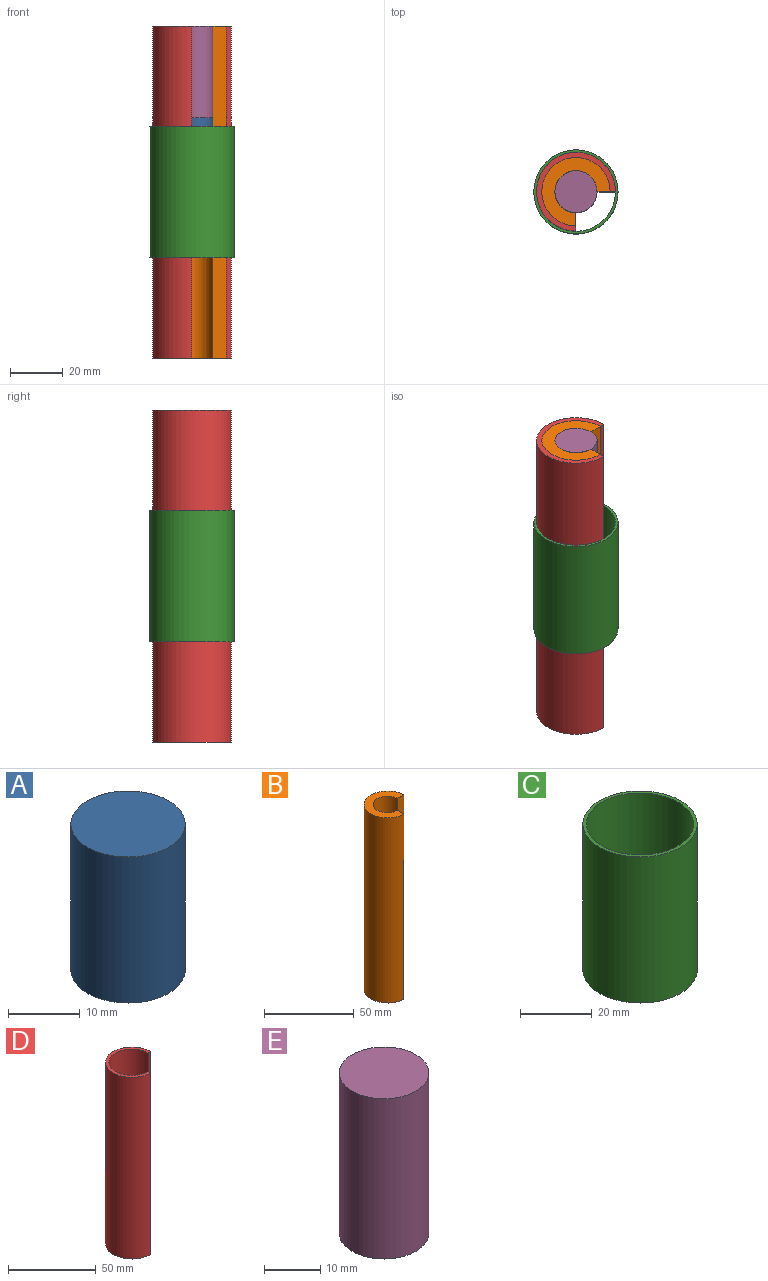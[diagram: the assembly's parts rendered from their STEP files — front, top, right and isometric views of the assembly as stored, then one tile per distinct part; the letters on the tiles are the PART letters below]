
ASSEMBLY  parts=5 mates=6
PART A: 3 faces, bbox 16x16x25 mm
  f0: cylinder r=8mm len=25mm, axis (0,0,-1), area 1256.6mm2, adj f1,f2
  f1: plane 16x16mm, normal (0,0,1), area 201.1mm2, adj f0
  f2: plane 16x16mm, normal (0,0,-1), area 201.1mm2, adj f0
PART B: 6 faces, bbox 26x26x126.3 mm
  f0: plane 26x26mm, normal (0,0,1), area 247.4mm2, adj f1,f3,f4,f5
  f1: cylinder r=8mm len=126.34mm, axis (0,0,-1), area 4762.8mm2, adj f0,f2,f4,f5
  f2: plane 26x26mm, normal (0,0,-1), area 247.4mm2, adj f1,f3,f4,f5
  f3: cylinder r=13mm len=126.34mm, axis (0,0,-1), area 7739.6mm2, adj f0,f2,f4,f5
  f4: plane 126.34x5mm, normal (1,0,0), area 631.7mm2, adj f0,f1,f2,f3
  f5: plane 126.34x5mm, normal (0,-1,0), area 631.7mm2, adj f0,f1,f2,f3
PART C: 4 faces, bbox 32x32x50 mm
  f0: cylinder r=16mm len=50mm, axis (0,0,1), area 5026.5mm2, adj f1,f2
  f1: plane 32x32mm, normal (0,0,-1), area 97.4mm2, adj f0,f3
  f2: plane 32x32mm, normal (0,0,1), area 97.4mm2, adj f0,f3
  f3: cylinder r=15mm len=50mm, axis (0,0,1), area 4712.4mm2, adj f1,f2
PART D: 6 faces, bbox 30x30x126.3 mm
  f0: plane 30x30mm, normal (0,0,1), area 131.9mm2, adj f1,f3,f4,f5
  f1: cylinder r=13mm len=126.34mm, axis (0,0,-1), area 7739.6mm2, adj f0,f2,f4,f5
  f2: plane 30x30mm, normal (0,0,-1), area 131.9mm2, adj f1,f3,f4,f5
  f3: cylinder r=15mm len=126.34mm, axis (0,0,-1), area 8930.3mm2, adj f0,f2,f4,f5
  f4: plane 126.34x2mm, normal (1,0,0), area 252.7mm2, adj f0,f1,f2,f3
  f5: plane 126.34x2mm, normal (0,-1,0), area 252.7mm2, adj f0,f1,f2,f3
PART E: 3 faces, bbox 16x16x35 mm
  f0: cylinder r=8mm len=35mm, axis (0,0,-1), area 1759.3mm2, adj f1,f2
  f1: plane 16x16mm, normal (0,0,1), area 201.1mm2, adj f0
  f2: plane 16x16mm, normal (0,0,-1), area 201.1mm2, adj f0
PLACE A t=(-31.66,-15.23,-57.09)mm
PLACE B t=(-31.66,-15.23,-66.47)mm
PLACE C t=(-31.66,-15.23,-35.26)mm
PLACE D t=(-31.66,-15.23,-66.47)mm
PLACE E t=(-31.66,-15.23,-32.09)mm
MATE planar E.f0 <-> B.f1  axis (0,0,-1) through (-31.66,-15.23,2.91)mm
MATE cylindrical C.f3 <-> D.f1  axis (0,0,1) through (-31.66,-15.23,-60.26)mm
MATE slider B.f1 <-> D.f1  axis (0,0,-1) through (-31.66,-15.23,-60.26)mm
MATE slider A.f0 <-> B.f1  axis (0,0,-1) through (-31.66,-15.23,-44.59)mm
MATE planar E.f0 <-> A.f0  axis (0,0,-1) through (-31.66,-15.23,-32.09)mm
MATE planar B.f2 <-> D.f2  axis (0,0,-1) through (-31.66,-28.23,-123.43)mm
